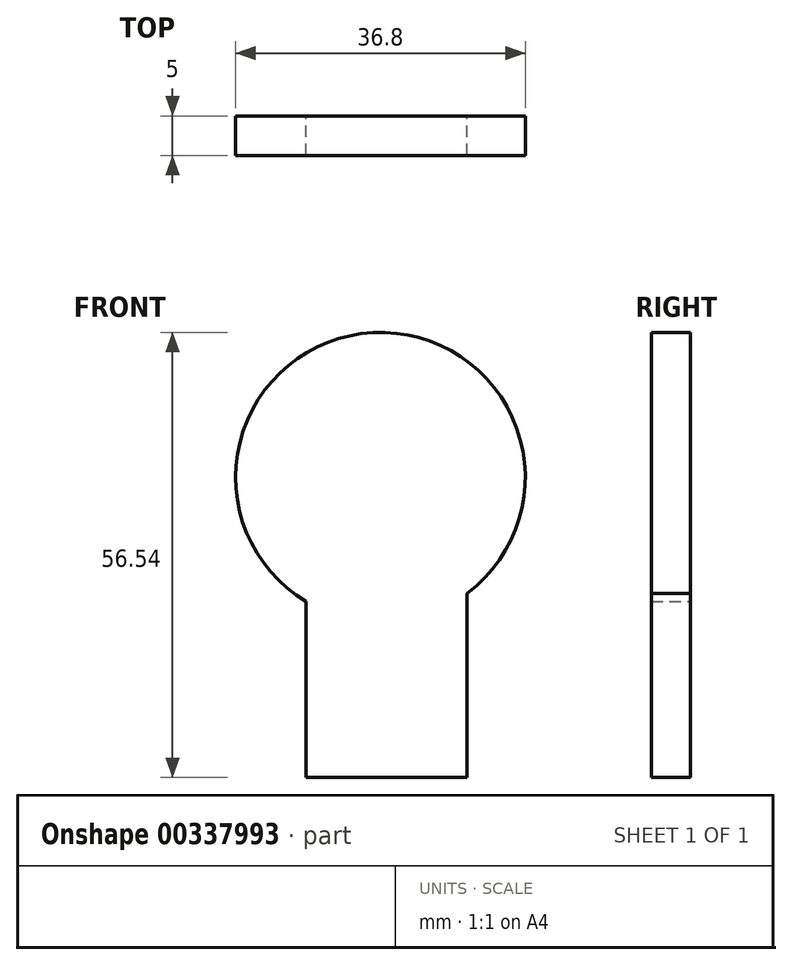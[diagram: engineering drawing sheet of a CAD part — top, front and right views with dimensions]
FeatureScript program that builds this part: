
annotation { "Feature Type Name" : "Feature", "Feature Type Description" : "" }
export const myFeature = defineFeature(function(context is Context, id is Id, definition is map)
    precondition{}
    {
        {
            var Q0;
            Q0=qCreatedBy(makeId("Front.planeOp"),FACE);
            var sketch = newSketch(context, id + "F0", { "sketchPlane" : qUnion([Q0])});
            skCircle(sketch, "E0", {"center": v(0, 0) * mm, "radius": 18.4 * mm});
            skLineSegment(sketch, "E1.bottom", {"start": v(11.02, 0) * mm, "end": v(-9.44, 0) * mm});
            skLineSegment(sketch, "E1.top", {"start": v(11.02, -38.14) * mm, "end": v(-9.44, -38.14) * mm});
            skLineSegment(sketch, "E1.left", {"start": v(11.02, 0) * mm, "end": v(11.02, -38.14) * mm});
            skLineSegment(sketch, "E1.right", {"start": v(-9.44, 0) * mm, "end": v(-9.44, -38.14) * mm});
            skSolve(sketch);
        }
        {
            var Q0;
            {var subQ5=sQuery(id+"F0.wireOp",EDGE,"E1.top");Q0=makeQuery(id+"F0.imprint","IMPRINT",FACE,{"disambiguationData":[TD([[makeQuery(id+"F0.imprint","IMPRINT",EDGE,{"derivedFrom":subQ5}),-1.0]])]});}
            var Q1;
            {var subQ5=sQuery(id+"F0.wireOp",EDGE,"E1.bottom");Q1=makeQuery(id+"F0.imprint","IMPRINT",FACE,{"disambiguationData":[TD([[makeQuery(id+"F0.imprint","IMPRINT",EDGE,{"derivedFrom":subQ5}),1.0]])]});}
            var Q2;
            {var subQ5=sQuery(id+"F0.wireOp",EDGE,"E1.bottom");Q2=makeQuery(id+"F0.imprint","IMPRINT",FACE,{"disambiguationData":[TD([[makeQuery(id+"F0.imprint","IMPRINT",EDGE,{"derivedFrom":subQ5}),-1.0]])]});}
            extrude(context, id + "F1", {"entities" : qUnion([Q0, Q1, Q2]), "depth" : 5 * mm});
        }
    });
